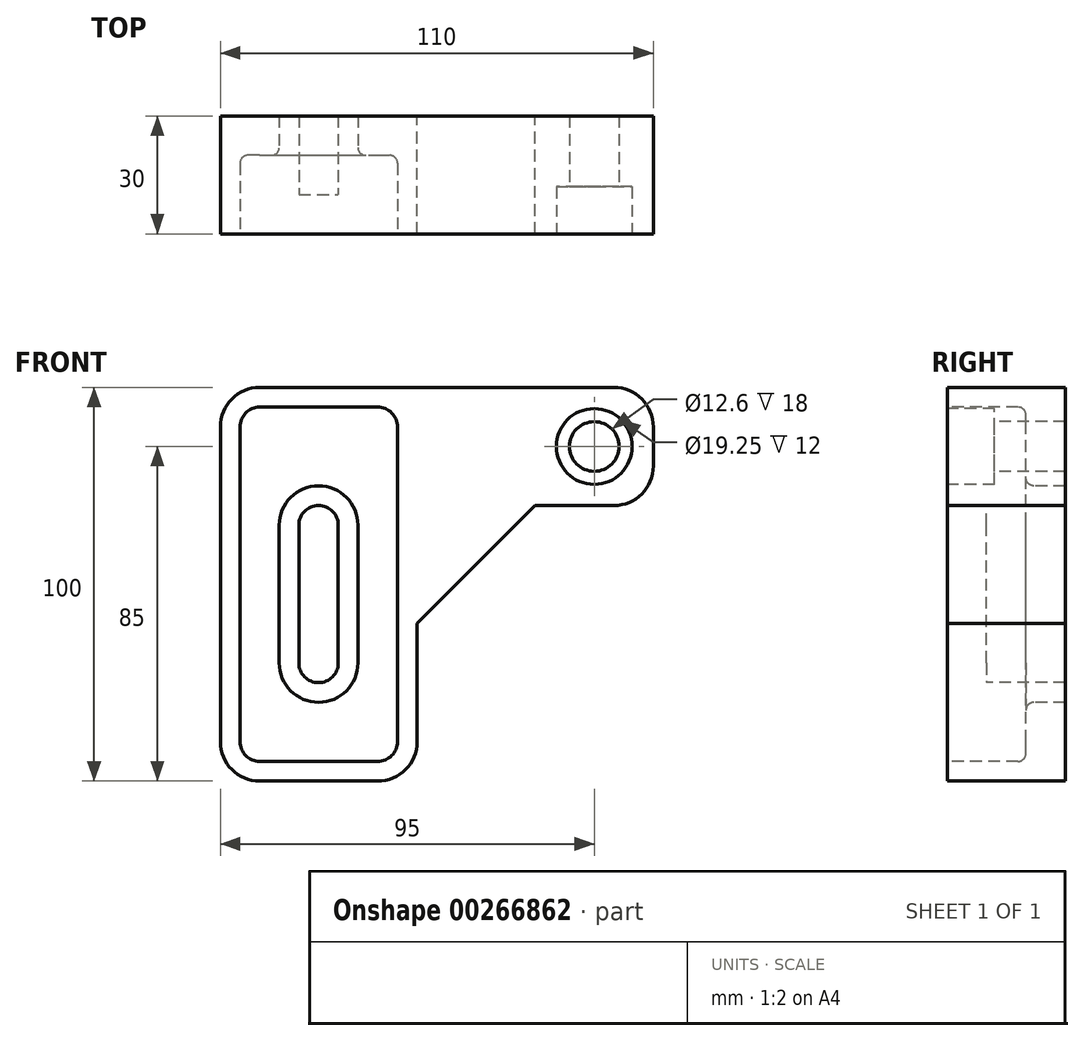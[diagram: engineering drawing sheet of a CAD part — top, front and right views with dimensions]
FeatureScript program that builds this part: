
annotation { "Feature Type Name" : "Feature", "Feature Type Description" : "" }
export const myFeature = defineFeature(function(context is Context, id is Id, definition is map)
    precondition{}
    {
        {
            var Q0;
            Q0=qCreatedBy(makeId("Front.planeOp"),FACE);
            var sketch = newSketch(context, id + "F0", { "sketchPlane" : qUnion([Q0])});
            skLineSegment(sketch, "E0", {"start": v(0, 0) * mm, "end": v(30, 30) * mm});
            skLineSegment(sketch, "E1", {"start": v(30, 30) * mm, "end": v(50, 30) * mm});
            skLineSegment(sketch, "E2", {"start": v(60, 40) * mm, "end": v(60, 50) * mm});
            skLineSegment(sketch, "E3", {"start": v(50, 60) * mm, "end": v(-40, 60) * mm});
            skLineSegment(sketch, "E4", {"start": v(-50, 50) * mm, "end": v(-50, -30) * mm});
            skLineSegment(sketch, "E5", {"start": v(-40, -40) * mm, "end": v(-10, -40) * mm});
            skLineSegment(sketch, "E6", {"start": v(0, -30) * mm, "end": v(0, 0) * mm});
            skLineSegment(sketch, "E7", {"start": v(0, 0) * mm, "end": v(0, 32.8) * mm, "construction": true});
            skPoint(sketch, "E8.visualSharp", {"position": v(60, 60) * mm});
            skArc(sketch, "E8.filletArc", {"start": v(60, 50) * mm, "mid": v(57.07, 57.07) * mm, "end": v(50, 60) * mm});
            skPoint(sketch, "E9.visualSharp", {"position": v(-50, 60) * mm});
            skArc(sketch, "E9.filletArc", {"start": v(-40, 60) * mm, "mid": v(-47.07, 57.07) * mm, "end": v(-50, 50) * mm});
            skPoint(sketch, "E10.visualSharp", {"position": v(-50, -40) * mm});
            skArc(sketch, "E10.filletArc", {"start": v(-50, -30) * mm, "mid": v(-47.07, -37.07) * mm, "end": v(-40, -40) * mm});
            skPoint(sketch, "E11.visualSharp", {"position": v(60, 30) * mm});
            skArc(sketch, "E11.filletArc", {"start": v(50, 30) * mm, "mid": v(57.07, 32.93) * mm, "end": v(60, 40) * mm});
            skPoint(sketch, "E12.visualSharp", {"position": v(0, -40) * mm});
            skArc(sketch, "E12.filletArc", {"start": v(-10, -40) * mm, "mid": v(-2.93, -37.07) * mm, "end": v(0, -30) * mm});
            skLineSegment(sketch, "E13", {"start": v(0, 32.8) * mm, "end": v(0, 60) * mm, "construction": true});
            skPoint(sketch, "E14", {"position": v(0, 60) * mm});
            skSolve(sketch);
        }
        {
            var Q0;
            Q0 = qSketchRegion(id + "F0", true);
            extrude(context, id + "F1", {"entities" : qUnion([Q0]), "depth" : 30 * mm});
        }
        {
            var Q0;
            Q0=makeQuery(id+"F1.opExtrude","CAP_FACE",FACE,{"disambiguationData":[OSD([sQuery(id+"F0.wireOp",EDGE,"E0"),sQuery(id+"F0.wireOp",EDGE,"E1"),sQuery(id+"F0.wireOp",EDGE,"E2"),sQuery(id+"F0.wireOp",EDGE,"E3"),sQuery(id+"F0.wireOp",EDGE,"E4"),sQuery(id+"F0.wireOp",EDGE,"E5"),sQuery(id+"F0.wireOp",EDGE,"E6"),sQuery(id+"F0.wireOp",EDGE,"E8.filletArc"),sQuery(id+"F0.wireOp",EDGE,"E9.filletArc"),sQuery(id+"F0.wireOp",EDGE,"E10.filletArc"),sQuery(id+"F0.wireOp",EDGE,"E11.filletArc"),sQuery(id+"F0.wireOp",EDGE,"E12.filletArc")])],"isStart":false});
            var sketch = newSketch(context, id + "F2", { "sketchPlane" : qUnion([Q0])});
            skCircle(sketch, "E15", {"center": v(45, 45) * mm, "radius": 7.41 * mm});
            skSolve(sketch);
        }
        {
            var Q0;
            Q0=sQuery(id+"F2.wireOp",VERTEX,"E15.center");
            var Q1;
            Q1=makeQuery(id+"F1.opExtrude","SWEPT_BODY",BODY,{"disambiguationData":[OSD([sQuery(id+"F0.wireOp",EDGE,"E0"),sQuery(id+"F0.wireOp",EDGE,"E1"),sQuery(id+"F0.wireOp",EDGE,"E2"),sQuery(id+"F0.wireOp",EDGE,"E3"),sQuery(id+"F0.wireOp",EDGE,"E4"),sQuery(id+"F0.wireOp",EDGE,"E5"),sQuery(id+"F0.wireOp",EDGE,"E6"),sQuery(id+"F0.wireOp",EDGE,"E8.filletArc"),sQuery(id+"F0.wireOp",EDGE,"E9.filletArc"),sQuery(id+"F0.wireOp",EDGE,"E10.filletArc"),sQuery(id+"F0.wireOp",EDGE,"E11.filletArc"),sQuery(id+"F0.wireOp",EDGE,"E12.filletArc")])]});
            hole(context, id + "F3", {"style" : HoleStyle.C_BORE, "endStyle" : HoleEndStyle.THROUGH, "standardTappedOrClearance" : lookupTablePath({ "standard" : "ISO", "fit" : "Close", "size" : "M12", "type" : "Clearance" }), "standardBlindInLast" : lookupTablePath({ "fit" : "Close", "standard" : "ISO", "size" : "M12", "type" : "Clearance" }), "holeDiameter" : 12.6 * mm, "cBoreDiameter" : 19.25 * mm, "cBoreDepth" : 12 * mm, "tappedDepth" : 12 * mm, "tapClearance" : 3, "locations" : qUnion([Q0]), "scope" : qUnion([Q1])});
        }
        {
            var Q0;
            Q0=makeQuery(id+"F1.opExtrude","CAP_FACE",FACE,{"disambiguationData":[OSD([sQuery(id+"F0.wireOp",EDGE,"E0"),sQuery(id+"F0.wireOp",EDGE,"E1"),sQuery(id+"F0.wireOp",EDGE,"E2"),sQuery(id+"F0.wireOp",EDGE,"E3"),sQuery(id+"F0.wireOp",EDGE,"E4"),sQuery(id+"F0.wireOp",EDGE,"E5"),sQuery(id+"F0.wireOp",EDGE,"E6"),sQuery(id+"F0.wireOp",EDGE,"E8.filletArc"),sQuery(id+"F0.wireOp",EDGE,"E9.filletArc"),sQuery(id+"F0.wireOp",EDGE,"E10.filletArc"),sQuery(id+"F0.wireOp",EDGE,"E11.filletArc"),sQuery(id+"F0.wireOp",EDGE,"E12.filletArc")])],"isStart":false});
            var sketch = newSketch(context, id + "F4", { "sketchPlane" : qUnion([Q0])});
            skLineSegment(sketch, "E16.0.0", {"start": v(-10, 60) * mm, "end": v(-40, 60) * mm});
            skArc(sketch, "E16.0.1", {"start": v(-40, 60) * mm, "mid": v(-47.07, 57.07) * mm, "end": v(-50, 50) * mm});
            skLineSegment(sketch, "E16.0.2", {"start": v(-50, 50) * mm, "end": v(-50, -30) * mm});
            skArc(sketch, "E16.0.3", {"start": v(-50, -30) * mm, "mid": v(-47.07, -37.07) * mm, "end": v(-40, -40) * mm});
            skLineSegment(sketch, "E16.0.4", {"start": v(-40, -40) * mm, "end": v(-10, -40) * mm});
            skArc(sketch, "E16.0.5", {"start": v(-10, -40) * mm, "mid": v(-2.93, -37.07) * mm, "end": v(0, -30) * mm});
            skLineSegment(sketch, "E16.0.6", {"start": v(0, -30) * mm, "end": v(0, 0) * mm});
            skLineSegment(sketch, "E16.0.7", {"start": v(0, 0) * mm, "end": v(30, 30) * mm});
            skLineSegment(sketch, "E16.0.8", {"start": v(30, 30) * mm, "end": v(50, 30) * mm});
            skArc(sketch, "E16.0.9", {"start": v(50, 30) * mm, "mid": v(57.07, 32.93) * mm, "end": v(60, 40) * mm});
            skLineSegment(sketch, "E16.0.10", {"start": v(60, 40) * mm, "end": v(60, 50) * mm});
            skArc(sketch, "E16.0.11", {"start": v(60, 50) * mm, "mid": v(57.07, 57.07) * mm, "end": v(50, 60) * mm});
            skLineSegment(sketch, "E17", {"start": v(0, 0) * mm, "end": v(0, 50) * mm, "construction": true});
            skPoint(sketch, "E18.newPointA", {"position": v(50, 60) * mm});
            skArc(sketch, "E18.filletArc", {"start": v(0, 50) * mm, "mid": v(-2.93, 57.07) * mm, "end": v(-10, 60) * mm});
            skLineSegment(sketch, "E19.0", {"start": v(-5, 0) * mm, "end": v(-5, 50) * mm});
            skLineSegment(sketch, "E19.1", {"start": v(-5, -30) * mm, "end": v(-5, 0) * mm});
            skArc(sketch, "E19.2", {"start": v(-5, 50) * mm, "mid": v(-6.46, 53.54) * mm, "end": v(-10, 55) * mm});
            skArc(sketch, "E19.3", {"start": v(-10, -35) * mm, "mid": v(-6.46, -33.54) * mm, "end": v(-5, -30) * mm});
            skLineSegment(sketch, "E19.4", {"start": v(-40, -35) * mm, "end": v(-10, -35) * mm});
            skLineSegment(sketch, "E19.5", {"start": v(-10, 55) * mm, "end": v(-40, 55) * mm});
            skArc(sketch, "E19.6", {"start": v(-40, 55) * mm, "mid": v(-43.54, 53.54) * mm, "end": v(-45, 50) * mm});
            skLineSegment(sketch, "E19.7", {"start": v(-45, 50) * mm, "end": v(-45, -30) * mm});
            skArc(sketch, "E19.8", {"start": v(-45, -30) * mm, "mid": v(-43.54, -33.54) * mm, "end": v(-40, -35) * mm});
            skSolve(sketch);
        }
        {
            var Q0;
            Q0=makeQuery(id+"F4.imprint","IMPRINT",FACE,{"disambiguationData":[TD([[makeQuery(id+"F4.imprint","IMPRINT",EDGE,{"derivedFrom":sQuery(id+"F4.wireOp",EDGE,"E19.0")}),1.0]])]});
            var Q1;
            Q1=sQuery(id+"F4.wireOp",EDGE,"E19.0");
            var Q2;
            Q2=sQuery(id+"F4.wireOp",EDGE,"E19.1");
            var Q3;
            Q3=sQuery(id+"F4.wireOp",EDGE,"E19.2");
            var Q4;
            Q4=sQuery(id+"F4.wireOp",EDGE,"E19.3");
            var Q5;
            Q5=sQuery(id+"F4.wireOp",EDGE,"E19.4");
            var Q6;
            Q6=sQuery(id+"F4.wireOp",EDGE,"E19.5");
            var Q7;
            Q7=sQuery(id+"F4.wireOp",EDGE,"E19.6");
            var Q8;
            Q8=sQuery(id+"F4.wireOp",EDGE,"E19.7");
            var Q9;
            Q9=sQuery(id+"F4.wireOp",EDGE,"E19.8");
            extrude(context, id + "F5", {"entities" : qUnion([Q0]), "operationType" : NewBodyOperationType.REMOVE, "surfaceEntities" : qUnion([Q1, Q2, Q3, Q4, Q5, Q6, Q7, Q8, Q9]), "oppositeDirection" : true, "depth" : 20 * mm});
        }
        {
            var Q0;
            Q0=makeQuery(id+"F5.boolean.opBoolean","COPY",FACE,{"derivedFrom":makeQuery(id+"F5.opExtrude","CAP_FACE",FACE,{"disambiguationData":[OSD([sQuery(id+"F4.wireOp",EDGE,"E19.0"),sQuery(id+"F4.wireOp",EDGE,"E19.1"),sQuery(id+"F4.wireOp",EDGE,"E19.2"),sQuery(id+"F4.wireOp",EDGE,"E19.3"),sQuery(id+"F4.wireOp",EDGE,"E19.4"),sQuery(id+"F4.wireOp",EDGE,"E19.5"),sQuery(id+"F4.wireOp",EDGE,"E19.6"),sQuery(id+"F4.wireOp",EDGE,"E19.7"),sQuery(id+"F4.wireOp",EDGE,"E19.8")])],"isStart":false})});
            var sketch = newSketch(context, id + "F6", { "sketchPlane" : qUnion([Q0])});
            skPoint(sketch, "E20", {"position": v(-15.84, -13.93) * mm});
            skLineSegment(sketch, "E21", {"start": v(-25.04, -10) * mm, "end": v(-25.04, 25) * mm, "construction": true});
            skArc(sketch, "E22.0.startCap", {"start": v(-15.04, -10) * mm, "mid": v(-25.04, -20) * mm, "end": v(-35.04, -10) * mm});
            skArc(sketch, "E22.0.endCap", {"start": v(-35.04, 25) * mm, "mid": v(-25.04, 35) * mm, "end": v(-15.04, 25) * mm});
            skLineSegment(sketch, "E22.0.left", {"start": v(-35.04, -10) * mm, "end": v(-35.04, 25) * mm});
            skLineSegment(sketch, "E22.0.right", {"start": v(-15.04, -10) * mm, "end": v(-15.04, 25) * mm});
            skSolve(sketch);
        }
        {
            var Q0;
            Q0 = qSketchRegion(id + "F6", true);
            extrude(context, id + "F7", {"entities" : qUnion([Q0]), "operationType" : NewBodyOperationType.ADD, "depth" : 10 * mm});
        }
        {
            var Q0;
            Q0=makeQuery(id+"F7.opExtrude","CAP_FACE",FACE,{"disambiguationData":[OSD([sQuery(id+"F6.wireOp",EDGE,"E22.0.startCap"),sQuery(id+"F6.wireOp",EDGE,"E22.0.endCap"),sQuery(id+"F6.wireOp",EDGE,"E22.0.left"),sQuery(id+"F6.wireOp",EDGE,"E22.0.right")])],"isStart":false});
            var sketch = newSketch(context, id + "F8", { "sketchPlane" : qUnion([Q0])});
            skLineSegment(sketch, "E23.0", {"start": v(-25.04, -10) * mm, "end": v(-25.04, 25) * mm, "construction": true});
            skArc(sketch, "E24.0.startCap", {"start": v(-20.04, -10) * mm, "mid": v(-25.04, -15) * mm, "end": v(-30.04, -10) * mm});
            skArc(sketch, "E24.0.endCap", {"start": v(-30.04, 25) * mm, "mid": v(-25.04, 30) * mm, "end": v(-20.04, 25) * mm});
            skLineSegment(sketch, "E24.0.left", {"start": v(-30.04, -10) * mm, "end": v(-30.04, 25) * mm});
            skLineSegment(sketch, "E24.0.right", {"start": v(-20.04, -10) * mm, "end": v(-20.04, 25) * mm});
            skSolve(sketch);
        }
        {
            var Q0;
            Q0=makeQuery(id+"F8.imprint","IMPRINT",FACE,{"disambiguationData":[TD([[makeQuery(id+"F8.imprint","IMPRINT",EDGE,{"derivedFrom":sQuery(id+"F8.wireOp",EDGE,"E24.0.startCap")}),-1.0]])]});
            var Q1;
            Q1=sQuery(id+"F8.wireOp",EDGE,"E24.0.left");
            extrude(context, id + "F9", {"entities" : qUnion([Q0]), "operationType" : NewBodyOperationType.REMOVE, "surfaceEntities" : qUnion([Q1]), "endBound" : BoundingType.SYMMETRIC, "oppositeDirection" : true, "depth" : 103 * mm});
        }
        {
            var Q0;
            Q0=makeQuery(id+"F5.boolean.opBoolean","COPY",FACE,{"derivedFrom":makeQuery(id+"F5.opExtrude","CAP_FACE",FACE,{"disambiguationData":[OSD([sQuery(id+"F4.wireOp",EDGE,"E19.0"),sQuery(id+"F4.wireOp",EDGE,"E19.1"),sQuery(id+"F4.wireOp",EDGE,"E19.2"),sQuery(id+"F4.wireOp",EDGE,"E19.3"),sQuery(id+"F4.wireOp",EDGE,"E19.4"),sQuery(id+"F4.wireOp",EDGE,"E19.5"),sQuery(id+"F4.wireOp",EDGE,"E19.6"),sQuery(id+"F4.wireOp",EDGE,"E19.7"),sQuery(id+"F4.wireOp",EDGE,"E19.8")])],"isStart":false})});
            fillet(context, id + "F10", {"entities" : qUnion([Q0]), "radius" : 2 * mm, "tangentPropagation" : true, "allowEdgeOverflow" : false});
        }
    });
